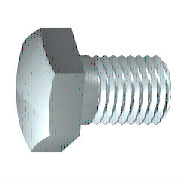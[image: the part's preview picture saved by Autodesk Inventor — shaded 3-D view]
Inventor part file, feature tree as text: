
AUTODESK INVENTOR PART (.ipt)
format: ipt  version: 2021 (Build 250183000, 183)  size: 194,560 bytes
history: native  units: mm (DEFAULTED — no unit token found)
features: sketch x3, extrude x1, chamfer x1, plane x1
ambient origin geometry x7: Origin, YZ Plane, XZ Plane, X Axis, Y Axis, Z Axis, Center Point
bodies: Solid1 (feature_tree), Body (feature_tree)
feature tree (6):
  extrude  "Head"  Depth=9.9mm
  chamfer  "Chamfer1"  Distance=2.4mm
  plane  "Work Plane1"
  sketch  "Sketch1"  dims[d0=12.0mm d1=9.9mm]
  sketch  "Sketch2"  dims[d2=4.0mm]
  sketch  "Sketch4"  dims[d12=90.0deg d3=2.4mm d4=0.0mm d5=30.0deg d21=90.0deg d6=0.429415mm d7=0.429515mm d8=0.0mm d9=0.4001mm d10=6.03mm d11=7.0mm d13=0.429515mm d14=4.0mm d15=9.9mm d16=0.0mm d19=7.0mm d55=45.0deg d57=0.0mm d58=0.0mm]
